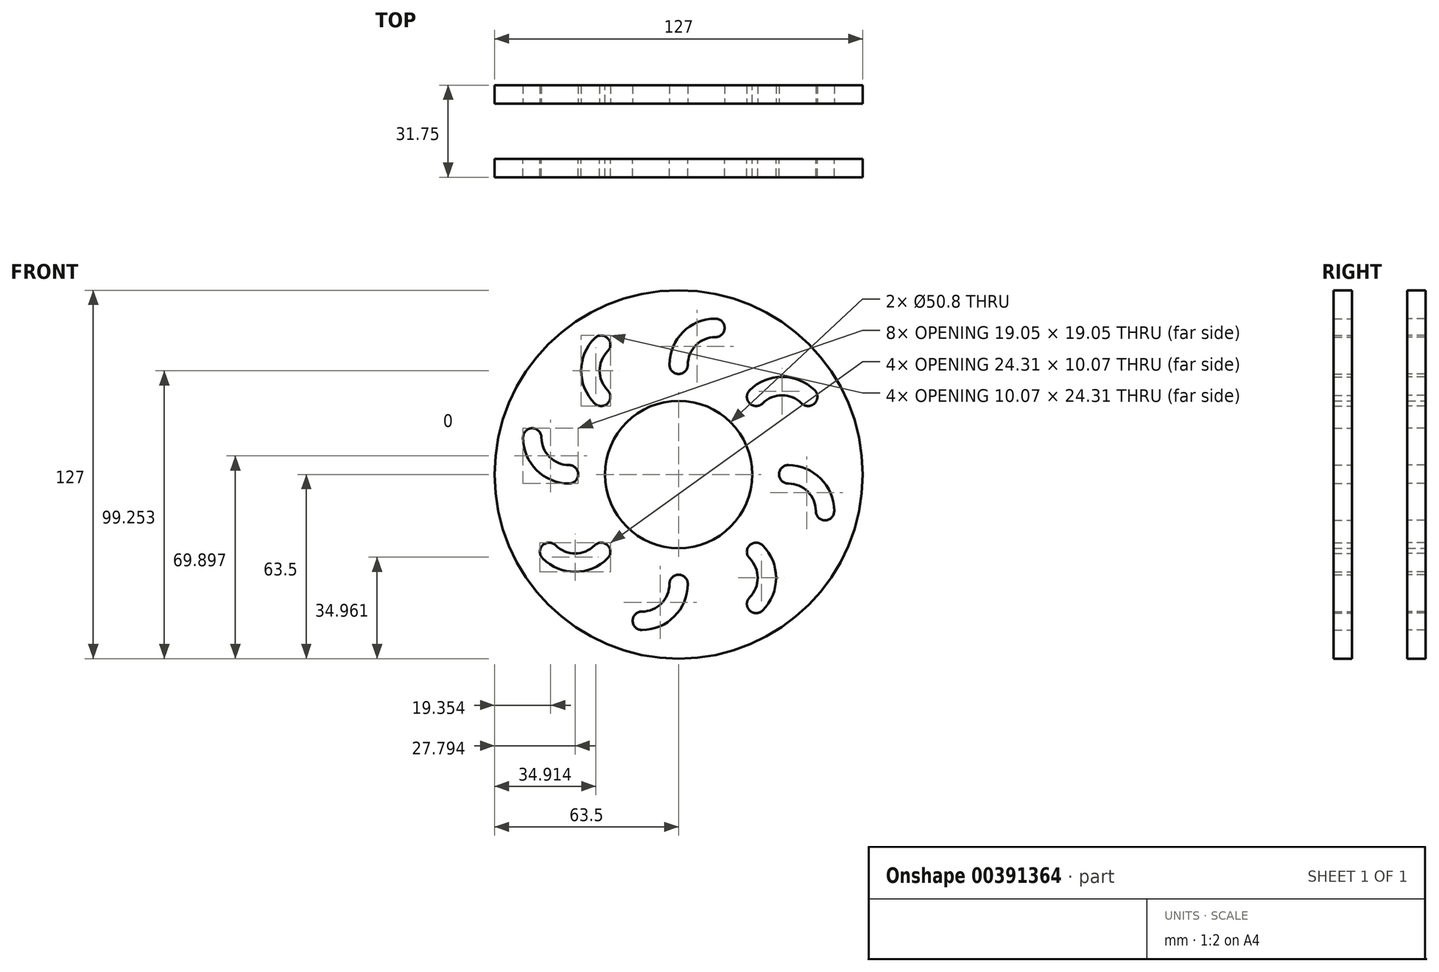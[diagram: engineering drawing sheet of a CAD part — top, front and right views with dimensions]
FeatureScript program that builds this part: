
annotation { "Feature Type Name" : "Feature", "Feature Type Description" : "" }
export const myFeature = defineFeature(function(context is Context, id is Id, definition is map)
    precondition{}
    {
        {
            var Q0;
            Q0=qCreatedBy(makeId("Front.planeOp"),FACE);
            var sketch = newSketch(context, id + "F0", { "sketchPlane" : qUnion([Q0])});
            skCircle(sketch, "E0", {"center": v(0, 0) * mm, "radius": 63.5 * mm});
            skCircle(sketch, "E1", {"center": v(0, 0) * mm, "radius": 25.4 * mm});
            skSolve(sketch);
        }
        {
            var Q0;
            Q0=makeQuery(id+"F0.imprint","IMPRINT",FACE,{"disambiguationData":[TD([[makeQuery(id+"F0.imprint","IMPRINT",EDGE,{"derivedFrom":sQuery(id+"F0.wireOp",EDGE,"E0")}),1.0]])]});
            extrude(context, id + "F1", {"entities" : qUnion([Q0]), "depth" : 6.35 * mm, "offsetDistance" : 25.4 * mm});
        }
        {
            var Q0;
            Q0=makeQuery(id+"F1.opExtrude","CAP_FACE",FACE,{"disambiguationData":[OSD([sQuery(id+"F0.wireOp",EDGE,"E0"),sQuery(id+"F0.wireOp",EDGE,"E1")])],"isStart":false});
            var sketch = newSketch(context, id + "F2", { "sketchPlane" : qUnion([Q0])});
            skArc(sketch, "E2", {"start": v(12.7, 50.54) * mm, "mid": v(3.72, 46.82) * mm, "end": v(0, 37.84) * mm});
            skArc(sketch, "E3.0.startCap", {"start": v(12.7, 53.72) * mm, "mid": v(15.88, 50.54) * mm, "end": v(12.7, 47.37) * mm});
            skArc(sketch, "E3.0.endCap", {"start": v(3.18, 37.84) * mm, "mid": v(0, 34.67) * mm, "end": v(-3.18, 37.84) * mm});
            skArc(sketch, "E3.0.left", {"start": v(12.7, 47.37) * mm, "mid": v(5.96, 44.58) * mm, "end": v(3.18, 37.84) * mm});
            skArc(sketch, "E3.0.right", {"start": v(12.7, 53.72) * mm, "mid": v(1.47, 49.07) * mm, "end": v(-3.18, 37.84) * mm});
            skLineSegment(sketch, "E4", {"start": v(0, 37.84) * mm, "end": v(12.7, 37.84) * mm, "construction": true});
            skLineSegment(sketch, "E5", {"start": v(12.7, 37.84) * mm, "end": v(12.7, 50.54) * mm, "construction": true});
            skArc(sketch, "E6.1.0", {"start": v(-24.48, 29.02) * mm, "mid": v(-24.48, 24.53) * mm, "end": v(-28.97, 24.53) * mm});
            skArc(sketch, "E6.1.1", {"start": v(-24.48, 42.49) * mm, "mid": v(-27.27, 35.75) * mm, "end": v(-24.48, 29.02) * mm});
            skArc(sketch, "E6.1.2", {"start": v(-28.97, 46.98) * mm, "mid": v(-33.62, 35.75) * mm, "end": v(-28.97, 24.53) * mm});
            skArc(sketch, "E6.1.3", {"start": v(-28.97, 46.98) * mm, "mid": v(-24.48, 46.98) * mm, "end": v(-24.48, 42.49) * mm});
            skArc(sketch, "E6.2.0", {"start": v(-37.8, 3.22) * mm, "mid": v(-34.62, 0.05) * mm, "end": v(-37.8, -3.13) * mm});
            skArc(sketch, "E6.2.1", {"start": v(-47.32, 12.75) * mm, "mid": v(-44.53, 6.01) * mm, "end": v(-37.8, 3.22) * mm});
            skArc(sketch, "E6.2.2", {"start": v(-53.67, 12.75) * mm, "mid": v(-49.02, 1.52) * mm, "end": v(-37.8, -3.13) * mm});
            skArc(sketch, "E6.2.3", {"start": v(-53.67, 12.75) * mm, "mid": v(-50.5, 15.92) * mm, "end": v(-47.32, 12.75) * mm});
            skArc(sketch, "E6.3.0", {"start": v(-28.97, -24.43) * mm, "mid": v(-24.48, -24.43) * mm, "end": v(-24.48, -28.92) * mm});
            skArc(sketch, "E6.3.1", {"start": v(-42.44, -24.43) * mm, "mid": v(-35.7, -27.22) * mm, "end": v(-28.97, -24.43) * mm});
            skArc(sketch, "E6.3.2", {"start": v(-46.93, -28.92) * mm, "mid": v(-35.7, -33.57) * mm, "end": v(-24.48, -28.92) * mm});
            skArc(sketch, "E6.3.3", {"start": v(-46.93, -28.92) * mm, "mid": v(-46.93, -24.43) * mm, "end": v(-42.44, -24.43) * mm});
            skArc(sketch, "E6.4.0", {"start": v(-3.18, -37.75) * mm, "mid": v(0, -34.57) * mm, "end": v(3.17, -37.75) * mm});
            skArc(sketch, "E6.4.1", {"start": v(-12.7, -47.27) * mm, "mid": v(-5.96, -44.48) * mm, "end": v(-3.18, -37.75) * mm});
            skArc(sketch, "E6.4.2", {"start": v(-12.7, -53.62) * mm, "mid": v(-1.47, -48.97) * mm, "end": v(3.17, -37.75) * mm});
            skArc(sketch, "E6.4.3", {"start": v(-12.7, -53.62) * mm, "mid": v(-15.88, -50.45) * mm, "end": v(-12.7, -47.27) * mm});
            skArc(sketch, "E6.5.0", {"start": v(24.48, -28.92) * mm, "mid": v(24.48, -24.43) * mm, "end": v(28.97, -24.43) * mm});
            skArc(sketch, "E6.5.1", {"start": v(24.48, -42.4) * mm, "mid": v(27.27, -35.66) * mm, "end": v(24.48, -28.92) * mm});
            skArc(sketch, "E6.5.2", {"start": v(28.97, -46.88) * mm, "mid": v(33.62, -35.66) * mm, "end": v(28.97, -24.43) * mm});
            skArc(sketch, "E6.5.3", {"start": v(28.97, -46.88) * mm, "mid": v(24.48, -46.88) * mm, "end": v(24.48, -42.4) * mm});
            skArc(sketch, "E6.6.0", {"start": v(37.8, -3.13) * mm, "mid": v(34.62, 0.05) * mm, "end": v(37.8, 3.22) * mm});
            skArc(sketch, "E6.6.1", {"start": v(47.32, -12.65) * mm, "mid": v(44.53, -5.92) * mm, "end": v(37.8, -3.13) * mm});
            skArc(sketch, "E6.6.2", {"start": v(53.67, -12.65) * mm, "mid": v(49.02, -1.43) * mm, "end": v(37.8, 3.22) * mm});
            skArc(sketch, "E6.6.3", {"start": v(53.67, -12.65) * mm, "mid": v(50.5, -15.83) * mm, "end": v(47.32, -12.65) * mm});
            skArc(sketch, "E6.7.0", {"start": v(28.97, 24.53) * mm, "mid": v(24.48, 24.53) * mm, "end": v(24.48, 29.02) * mm});
            skArc(sketch, "E6.7.1", {"start": v(42.44, 24.53) * mm, "mid": v(35.7, 27.32) * mm, "end": v(28.97, 24.53) * mm});
            skArc(sketch, "E6.7.2", {"start": v(46.93, 29.02) * mm, "mid": v(35.7, 33.67) * mm, "end": v(24.48, 29.02) * mm});
            skArc(sketch, "E6.7.3", {"start": v(46.93, 29.02) * mm, "mid": v(46.93, 24.53) * mm, "end": v(42.44, 24.53) * mm});
            skPoint(sketch, "E6.center", {"position": v(0, 0.05) * mm});
            skPoint(sketch, "E7", {"position": v(0, 63.5) * mm});
            skPoint(sketch, "E8", {"position": v(0, 25.4) * mm});
            skPoint(sketch, "E9", {"position": v(5.25, 55.15) * mm});
            skLineSegment(sketch, "E10", {"start": v(0, 63.5) * mm, "end": v(0, 25.4) * mm, "construction": true});
            skPoint(sketch, "E11", {"position": v(0, 44.45) * mm});
            skSolve(sketch);
        }
        {
            var Q0;
            Q0 = qSketchRegion(id + "F2", true);
            extrude(context, id + "F3", {"entities" : qUnion([Q0]), "operationType" : NewBodyOperationType.REMOVE, "oppositeDirection" : true, "depth" : 25.4 * mm, "offsetDistance" : 25.4 * mm});
        }
        {
            var Q0;
            Q0=qCreatedBy(makeId("Front.planeOp"),FACE);
            cPlane(context, id + "F4", {"entities" : qUnion([Q0]), "cplaneType" : CPlaneType.OFFSET, "offset" : 25.4 * mm, "width" : 152.4 * mm, "height" : 152.4 * mm});
        }
        {
            var Q0;
            Q0=qCreatedBy(id+"F4.planeOp",FACE);
            var sketch = newSketch(context, id + "F5", { "sketchPlane" : qUnion([Q0])});
            skCircle(sketch, "E12.0.0", {"center": v(0, 0) * mm, "radius": 63.5 * mm});
            skArc(sketch, "E13.0", {"start": v(-46.93, -28.92) * mm, "mid": v(-35.7, -33.57) * mm, "end": v(-24.48, -28.92) * mm});
            skArc(sketch, "E13.1", {"start": v(-46.93, -28.92) * mm, "mid": v(-46.93, -24.43) * mm, "end": v(-42.44, -24.43) * mm});
            skArc(sketch, "E13.2", {"start": v(-42.44, -24.43) * mm, "mid": v(-35.7, -27.22) * mm, "end": v(-28.97, -24.43) * mm});
            skArc(sketch, "E13.3", {"start": v(-28.97, -24.43) * mm, "mid": v(-24.48, -24.43) * mm, "end": v(-24.48, -28.92) * mm});
            skArc(sketch, "E13.4", {"start": v(-53.67, 12.75) * mm, "mid": v(-49.02, 1.52) * mm, "end": v(-37.8, -3.13) * mm});
            skArc(sketch, "E13.5", {"start": v(-37.8, 3.22) * mm, "mid": v(-34.62, 0.05) * mm, "end": v(-37.8, -3.13) * mm});
            skArc(sketch, "E13.6", {"start": v(-47.32, 12.75) * mm, "mid": v(-44.53, 6.01) * mm, "end": v(-37.8, 3.22) * mm});
            skArc(sketch, "E13.7", {"start": v(-53.67, 12.75) * mm, "mid": v(-50.5, 15.92) * mm, "end": v(-47.32, 12.75) * mm});
            skCircle(sketch, "E13.8", {"center": v(0, 0) * mm, "radius": 25.4 * mm});
            skArc(sketch, "E13.9", {"start": v(-12.7, -53.62) * mm, "mid": v(-15.88, -50.45) * mm, "end": v(-12.7, -47.27) * mm});
            skArc(sketch, "E13.10", {"start": v(-12.7, -47.27) * mm, "mid": v(-5.96, -44.48) * mm, "end": v(-3.18, -37.75) * mm});
            skArc(sketch, "E13.11", {"start": v(-3.18, -37.75) * mm, "mid": v(0, -34.57) * mm, "end": v(3.17, -37.75) * mm});
            skArc(sketch, "E13.12", {"start": v(-12.7, -53.62) * mm, "mid": v(-1.47, -48.97) * mm, "end": v(3.17, -37.75) * mm});
            skArc(sketch, "E13.13", {"start": v(24.48, -42.4) * mm, "mid": v(27.27, -35.66) * mm, "end": v(24.48, -28.92) * mm});
            skArc(sketch, "E13.14", {"start": v(24.48, -28.92) * mm, "mid": v(24.48, -24.43) * mm, "end": v(28.97, -24.43) * mm});
            skArc(sketch, "E13.15", {"start": v(28.97, -46.88) * mm, "mid": v(33.62, -35.66) * mm, "end": v(28.97, -24.43) * mm});
            skArc(sketch, "E13.16", {"start": v(28.97, -46.88) * mm, "mid": v(24.48, -46.88) * mm, "end": v(24.48, -42.4) * mm});
            skArc(sketch, "E13.17", {"start": v(53.67, -12.65) * mm, "mid": v(50.5, -15.83) * mm, "end": v(47.32, -12.65) * mm});
            skArc(sketch, "E13.18", {"start": v(47.32, -12.65) * mm, "mid": v(44.53, -5.92) * mm, "end": v(37.8, -3.13) * mm});
            skArc(sketch, "E13.19", {"start": v(53.67, -12.65) * mm, "mid": v(49.02, -1.43) * mm, "end": v(37.8, 3.22) * mm});
            skArc(sketch, "E13.20", {"start": v(37.8, -3.13) * mm, "mid": v(34.62, 0.05) * mm, "end": v(37.8, 3.22) * mm});
            skArc(sketch, "E13.21", {"start": v(46.93, 29.02) * mm, "mid": v(46.93, 24.53) * mm, "end": v(42.44, 24.53) * mm});
            skArc(sketch, "E13.22", {"start": v(28.97, 24.53) * mm, "mid": v(24.48, 24.53) * mm, "end": v(24.48, 29.02) * mm});
            skArc(sketch, "E13.23", {"start": v(42.44, 24.53) * mm, "mid": v(35.7, 27.32) * mm, "end": v(28.97, 24.53) * mm});
            skArc(sketch, "E13.24", {"start": v(46.93, 29.02) * mm, "mid": v(35.7, 33.67) * mm, "end": v(24.48, 29.02) * mm});
            skArc(sketch, "E13.25", {"start": v(3.18, 37.84) * mm, "mid": v(0, 34.67) * mm, "end": v(-3.18, 37.84) * mm});
            skArc(sketch, "E13.26", {"start": v(12.7, 53.72) * mm, "mid": v(1.47, 49.07) * mm, "end": v(-3.18, 37.84) * mm});
            skArc(sketch, "E13.27", {"start": v(12.7, 53.72) * mm, "mid": v(15.88, 50.54) * mm, "end": v(12.7, 47.37) * mm});
            skArc(sketch, "E13.28", {"start": v(12.7, 47.37) * mm, "mid": v(5.96, 44.58) * mm, "end": v(3.18, 37.84) * mm});
            skArc(sketch, "E13.29", {"start": v(-24.48, 29.02) * mm, "mid": v(-24.48, 24.53) * mm, "end": v(-28.97, 24.53) * mm});
            skArc(sketch, "E13.30", {"start": v(-28.97, 46.98) * mm, "mid": v(-33.62, 35.75) * mm, "end": v(-28.97, 24.53) * mm});
            skArc(sketch, "E13.31", {"start": v(-24.48, 42.49) * mm, "mid": v(-27.27, 35.75) * mm, "end": v(-24.48, 29.02) * mm});
            skArc(sketch, "E13.32", {"start": v(-28.97, 46.98) * mm, "mid": v(-24.48, 46.98) * mm, "end": v(-24.48, 42.49) * mm});
            skSolve(sketch);
        }
        {
            var Q0;
            Q0 = qSketchRegion(id + "F5", true);
            extrude(context, id + "F6", {"entities" : qUnion([Q0]), "depth" : 6.35 * mm, "offsetDistance" : 25.4 * mm});
        }
    });
